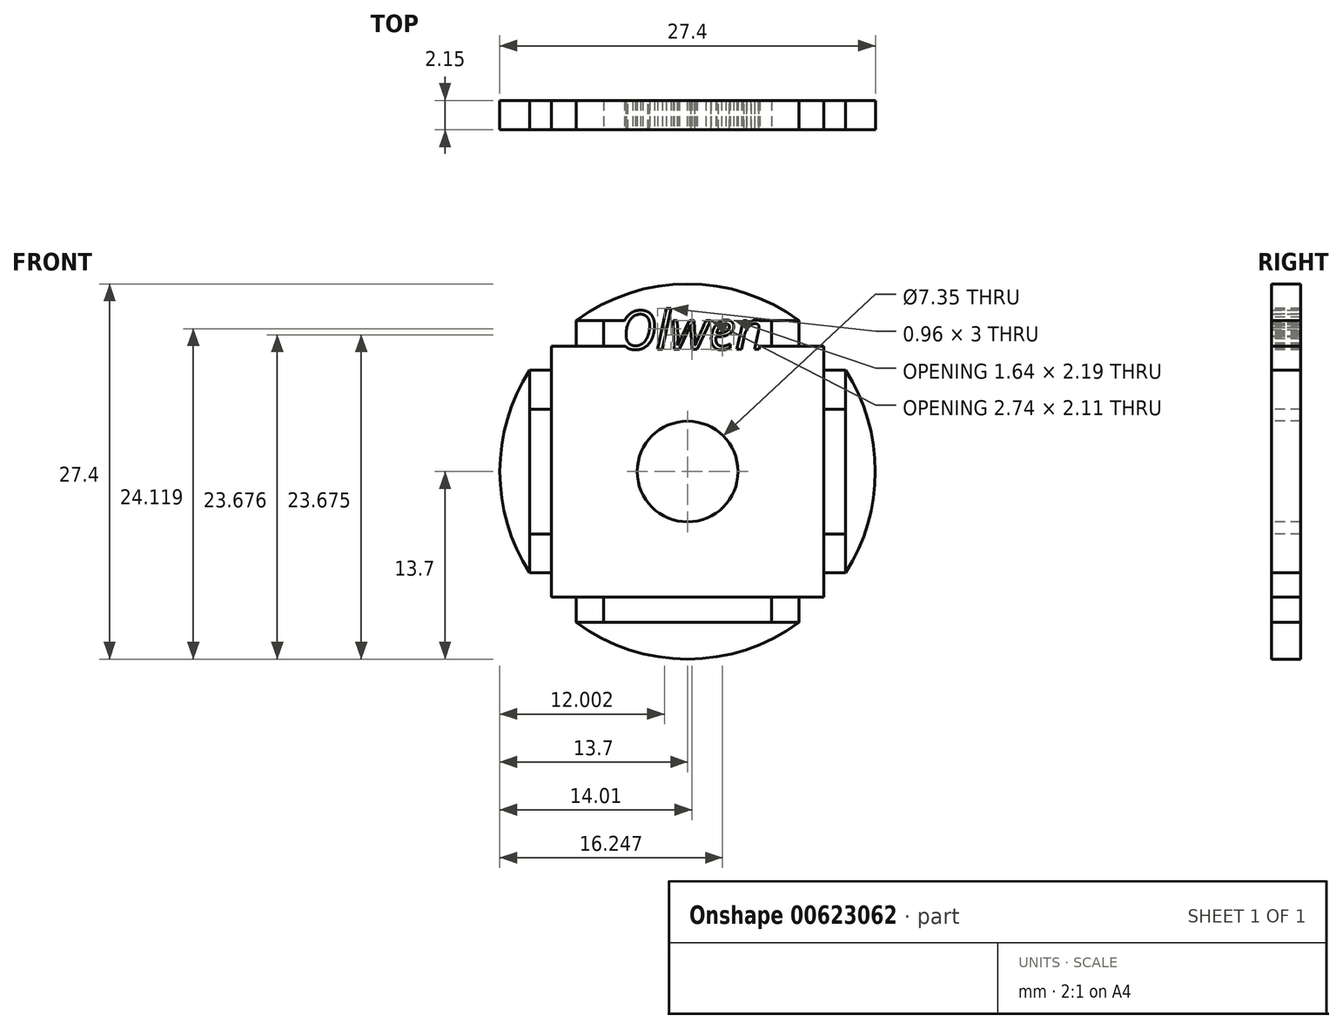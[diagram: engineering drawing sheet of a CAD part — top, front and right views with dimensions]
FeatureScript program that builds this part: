
annotation { "Feature Type Name" : "Feature", "Feature Type Description" : "" }
export const myFeature = defineFeature(function(context is Context, id is Id, definition is map)
    precondition{}
    {
        {
            var Q0;
            Q0=qCreatedBy(makeId("Front.planeOp"),FACE);
            var sketch = newSketch(context, id + "F0", { "sketchPlane" : qUnion([Q0])});
            skCircle(sketch, "E0", {"center": v(0, 0) * mm, "radius": 13.7 * mm});
            skSolve(sketch);
        }
        {
            var Q0;
            Q0=makeQuery(id+"F0.imprint","IMPRINT",FACE,{"disambiguationData":[TD([[makeQuery(id+"F0.imprint","IMPRINT",EDGE,{"derivedFrom":sQuery(id+"F0.wireOp",EDGE,"E0")}),1.0]])]});
            extrude(context, id + "F1", {"entities" : qUnion([Q0]), "depth" : 2.15 * mm, "offsetDistance" : 25 * mm});
        }
        {
            var Q0;
            Q0=makeQuery(id+"F1.opExtrude","CAP_FACE",FACE,{"disambiguationData":[OSD([sQuery(id+"F0.wireOp",EDGE,"E0")])],"isStart":false});
            var sketch = newSketch(context, id + "F2", { "sketchPlane" : qUnion([Q0])});
            skText(sketch, "E1", { "text": "Olwen", "fontName": "OpenSans-Italic.ttf"});
            const initialGuessF2  = {"E1": [-0.00513, 0.00892, 1, 0, 0.00284]};
            skSetInitialGuess(sketch, initialGuessF2);
            skSolve(sketch);
        }
        {
            var Q0;
            Q0 = qSketchRegion(id + "F2", true);
            extrude(context, id + "F3", {"entities" : qUnion([Q0]), "operationType" : NewBodyOperationType.REMOVE, "endBound" : BoundingType.UP_TO_NEXT, "oppositeDirection" : true, "depth" : 25 * mm, "offsetDistance" : 25 * mm});
        }
        {
            var Q0;
            {var subQ0=sQuery(id+"F0.wireOp",EDGE,"E0");Q0=makeQuery(id+"F3.boolean.opBoolean","SPLIT",FACE,{"disambiguationData":[TD([makeQuery(id+"F1.opExtrude","SWEPT_FACE",FACE,{"disambiguationData":[OSD([subQ0])]})])],"derivedFrom":makeQuery(id+"F1.opExtrude","CAP_FACE",FACE,{"disambiguationData":[OSD([subQ0])],"isStart":false})});}
            var sketch = newSketch(context, id + "F4", { "sketchPlane" : qUnion([Q0])});
            skCircle(sketch, "E2", {"center": v(0, 0) * mm, "radius": 3.68 * mm});
            skLineSegment(sketch, "E3.bottom", {"start": v(-6.75, 4.44) * mm, "end": v(6.75, 4.44) * mm});
            skLineSegment(sketch, "E3.top", {"start": v(-6.75, -4.44) * mm, "end": v(6.75, -4.44) * mm});
            skLineSegment(sketch, "E3.left", {"start": v(-6.75, 4.44) * mm, "end": v(-6.75, -4.44) * mm});
            skLineSegment(sketch, "E3.right", {"start": v(6.75, 4.44) * mm, "end": v(6.75, -4.44) * mm});
            skLineSegment(sketch, "E4.bottom", {"start": v(-1, 2.86) * mm, "end": v(1, 2.86) * mm});
            skLineSegment(sketch, "E4.top", {"start": v(-1, -2.86) * mm, "end": v(1, -2.86) * mm});
            skLineSegment(sketch, "E4.left", {"start": v(-1, 2.86) * mm, "end": v(-1, -2.86) * mm});
            skLineSegment(sketch, "E4.right", {"start": v(1, 2.86) * mm, "end": v(1, -2.86) * mm});
            skLineSegment(sketch, "E5.bottom", {"start": v(-8.86, 6.74) * mm, "end": v(8.86, 6.74) * mm});
            skLineSegment(sketch, "E5.top", {"start": v(-8.86, -6.74) * mm, "end": v(8.86, -6.74) * mm});
            skLineSegment(sketch, "E5.left", {"start": v(-8.86, 6.74) * mm, "end": v(-8.86, -6.74) * mm});
            skLineSegment(sketch, "E5.right", {"start": v(8.86, 6.74) * mm, "end": v(8.86, -6.74) * mm});
            skSolve(sketch);
        }
        {
            var Q0;
            Q0=makeQuery(id+"F4.imprint","IMPRINT",FACE,{"disambiguationData":[TD([[makeQuery(id+"F4.imprint","IMPRINT",EDGE,{"derivedFrom":sQuery(id+"F4.wireOp",EDGE,"E2")}),1.0]])]});
            var Q1;
            Q1=makeQuery(id+"F4.imprint","IMPRINT",FACE,{"disambiguationData":[TD([[makeQuery(id+"F4.imprint","IMPRINT",EDGE,{"derivedFrom":sQuery(id+"F4.wireOp",EDGE,"E4.bottom")}),-1.0]])]});
            extrude(context, id + "F5", {"entities" : qUnion([Q0, Q1]), "operationType" : NewBodyOperationType.REMOVE, "endBound" : BoundingType.UP_TO_NEXT, "oppositeDirection" : true, "depth" : 25 * mm, "offsetDistance" : 25 * mm});
        }
        {
            var Q0;
            {var subQ0=sQuery(id+"F0.wireOp",EDGE,"E0");Q0=makeQuery(id+"F3.boolean.opBoolean","SPLIT",FACE,{"disambiguationData":[TD([makeQuery(id+"F1.opExtrude","SWEPT_FACE",FACE,{"disambiguationData":[OSD([subQ0])]})])],"derivedFrom":makeQuery(id+"F1.opExtrude","CAP_FACE",FACE,{"disambiguationData":[OSD([subQ0])],"isStart":false})});}
            var sketch = newSketch(context, id + "F6", { "sketchPlane" : qUnion([Q0])});
            skLineSegment(sketch, "E6.bottom", {"start": v(-5.33, 4.8) * mm, "end": v(5.33, 4.8) * mm});
            skLineSegment(sketch, "E6.top", {"start": v(-5.33, -4.8) * mm, "end": v(5.33, -4.8) * mm});
            skLineSegment(sketch, "E6.left", {"start": v(-5.33, 4.8) * mm, "end": v(-5.33, -4.8) * mm});
            skLineSegment(sketch, "E6.right", {"start": v(5.33, 4.8) * mm, "end": v(5.33, -4.8) * mm});
            skPoint(sketch, "E6.middle", {"position": v(0, 0) * mm});
            skSolve(sketch);
        }
        {
            var Q0;
            {var subQ0=sQuery(id+"F0.wireOp",EDGE,"E0");Q0=makeQuery(id+"F3.boolean.opBoolean","SPLIT",FACE,{"disambiguationData":[TD([makeQuery(id+"F1.opExtrude","SWEPT_FACE",FACE,{"disambiguationData":[OSD([subQ0])]})])],"derivedFrom":makeQuery(id+"F1.opExtrude","CAP_FACE",FACE,{"disambiguationData":[OSD([subQ0])],"isStart":false})});}
            var sketch = newSketch(context, id + "F7", { "sketchPlane" : qUnion([Q0])});
            skLineSegment(sketch, "E7.0", {"start": v(-11.53, 11.03) * mm, "end": v(-11.53, -11.03) * mm});
            skLineSegment(sketch, "E7.1", {"start": v(11.53, 11.03) * mm, "end": v(-11.53, 11.03) * mm});
            skLineSegment(sketch, "E7.2", {"start": v(11.53, -11.03) * mm, "end": v(11.53, 11.03) * mm});
            skLineSegment(sketch, "E7.3", {"start": v(-11.53, -11.03) * mm, "end": v(11.53, -11.03) * mm});
            skSolve(sketch);
        }
        {
            var Q0;
            {var subQ3=makeQuery(id+"F3.boolean.opBoolean","COPY",EDGE,{"derivedFrom":makeQuery(id+"F3.opExtrude","CAP_EDGE",EDGE,{"disambiguationData":[OSD([sQuery(id+"F2.wireOp",EDGE,"E1.sketch_text.stroke-0")])],"isStart":true})});Q0=makeQuery(id+"F7.imprint","IMPRINT",FACE,{"disambiguationData":[TD([[makeQuery(id+"F7.imprint","IMPRINT",EDGE,{"derivedFrom":subQ3}),1.0]])]});}
            var sketch = newSketch(context, id + "F8", { "sketchPlane" : qUnion([Q0])});
            skLineSegment(sketch, "E8.bottom", {"start": v(-9.94, 9.16) * mm, "end": v(9.94, 9.16) * mm});
            skLineSegment(sketch, "E8.top", {"start": v(-9.94, -9.16) * mm, "end": v(9.94, -9.16) * mm});
            skLineSegment(sketch, "E8.left", {"start": v(-9.94, 9.16) * mm, "end": v(-9.94, -9.16) * mm});
            skLineSegment(sketch, "E8.right", {"start": v(9.94, 9.16) * mm, "end": v(9.94, -9.16) * mm});
            skPoint(sketch, "E8.middle", {"position": v(0, 0) * mm});
            skSolve(sketch);
        }
        {
            var Q0;
            Q0=makeQuery(id+"F8.imprint","IMPRINT",FACE,{"disambiguationData":[TD([[makeQuery(id+"F8.imprint","IMPRINT",EDGE,{"derivedFrom":sQuery(id+"F8.wireOp",EDGE,"E8.top")}),-1.0]])]});
            extrude(context, id + "F9", {"entities" : qUnion([Q0]), "operationType" : NewBodyOperationType.REMOVE, "endBound" : BoundingType.UP_TO_NEXT, "oppositeDirection" : true, "depth" : 25 * mm, "offsetDistance" : 25 * mm});
        }
        {
            var Q0;
            Q0=makeQuery(id+"F6.imprint","IMPRINT",FACE,{"disambiguationData":[TD([[makeQuery(id+"F6.imprint","IMPRINT",EDGE,{"derivedFrom":sQuery(id+"F6.wireOp",EDGE,"E6.bottom")}),1.0]])]});
            var sketch = newSketch(context, id + "F10", { "sketchPlane" : qUnion([Q0])});
            skLineSegment(sketch, "E9.bottom", {"start": v(-11.53, 7.4) * mm, "end": v(-9.94, 7.4) * mm});
            skLineSegment(sketch, "E9.top", {"start": v(-11.53, 4.56) * mm, "end": v(-9.94, 4.56) * mm});
            skLineSegment(sketch, "E9.left", {"start": v(-11.53, 7.4) * mm, "end": v(-11.53, 4.56) * mm});
            skLineSegment(sketch, "E9.right", {"start": v(-9.94, 7.4) * mm, "end": v(-9.94, 4.56) * mm});
            skLineSegment(sketch, "E10.MirrorCS", {"start": v(-11.53, -4.56) * mm, "end": v(-9.94, -4.56) * mm});
            skLineSegment(sketch, "E11.MirrorCS", {"start": v(-11.53, -7.4) * mm, "end": v(-9.94, -7.4) * mm});
            skLineSegment(sketch, "E12.MirrorCS", {"start": v(-9.94, -7.4) * mm, "end": v(-9.94, -4.56) * mm});
            skLineSegment(sketch, "E13.MirrorCS", {"start": v(-11.53, -7.4) * mm, "end": v(-11.53, -4.56) * mm});
            skLineSegment(sketch, "E14.MirrorCS", {"start": v(11.53, 7.4) * mm, "end": v(9.94, 7.4) * mm});
            skLineSegment(sketch, "E15.MirrorCS", {"start": v(11.53, -7.4) * mm, "end": v(11.53, -4.56) * mm});
            skLineSegment(sketch, "E16.MirrorCS", {"start": v(11.53, 4.56) * mm, "end": v(9.94, 4.56) * mm});
            skLineSegment(sketch, "E17.MirrorCS", {"start": v(9.94, 7.4) * mm, "end": v(9.94, 4.56) * mm});
            skLineSegment(sketch, "E18.MirrorCS", {"start": v(11.53, -4.56) * mm, "end": v(9.94, -4.56) * mm});
            skLineSegment(sketch, "E19.MirrorCS", {"start": v(11.53, -7.4) * mm, "end": v(9.94, -7.4) * mm});
            skLineSegment(sketch, "E20.MirrorCS", {"start": v(9.94, -7.4) * mm, "end": v(9.94, -4.56) * mm});
            skLineSegment(sketch, "E21.MirrorCS", {"start": v(11.53, 7.4) * mm, "end": v(11.53, 4.56) * mm});
            skSolve(sketch);
        }
        {
            var Q0;
            Q0=makeQuery(id+"F6.imprint","IMPRINT",FACE,{"disambiguationData":[TD([[makeQuery(id+"F6.imprint","IMPRINT",EDGE,{"derivedFrom":sQuery(id+"F6.wireOp",EDGE,"E6.bottom")}),1.0]])]});
            var sketch = newSketch(context, id + "F11", { "sketchPlane" : qUnion([Q0])});
            skLineSegment(sketch, "E22", {"start": v(-8.13, -9.16) * mm, "end": v(-6.13, -9.16) * mm});
            skLineSegment(sketch, "E23", {"start": v(-8.13, -9.16) * mm, "end": v(-8.13, -11.03) * mm});
            skLineSegment(sketch, "E24", {"start": v(-8.13, -11.03) * mm, "end": v(-6.13, -11.03) * mm});
            skLineSegment(sketch, "E25", {"start": v(-6.13, -11.03) * mm, "end": v(-6.13, -9.16) * mm});
            skLineSegment(sketch, "E26.MirrorCS", {"start": v(6.13, -11.03) * mm, "end": v(6.13, -9.16) * mm});
            skLineSegment(sketch, "E27.MirrorCS", {"start": v(8.13, -9.16) * mm, "end": v(6.13, -9.16) * mm});
            skLineSegment(sketch, "E28.MirrorCS", {"start": v(8.13, -11.03) * mm, "end": v(6.13, -11.03) * mm});
            skLineSegment(sketch, "E29.MirrorCS", {"start": v(8.13, -9.16) * mm, "end": v(8.13, -11.03) * mm});
            skLineSegment(sketch, "E30.MirrorCS", {"start": v(8.13, 9.16) * mm, "end": v(6.13, 9.16) * mm});
            skLineSegment(sketch, "E31.MirrorCS", {"start": v(6.13, 11.03) * mm, "end": v(6.13, 9.16) * mm});
            skLineSegment(sketch, "E32.MirrorCS", {"start": v(-6.13, 11.03) * mm, "end": v(-6.13, 9.16) * mm});
            skLineSegment(sketch, "E33.MirrorCS", {"start": v(-8.13, 9.16) * mm, "end": v(-6.13, 9.16) * mm});
            skLineSegment(sketch, "E34.MirrorCS", {"start": v(8.13, 9.16) * mm, "end": v(8.13, 11.03) * mm});
            skLineSegment(sketch, "E35.MirrorCS", {"start": v(-8.13, 11.03) * mm, "end": v(-6.13, 11.03) * mm});
            skLineSegment(sketch, "E36.MirrorCS", {"start": v(8.13, 11.03) * mm, "end": v(6.13, 11.03) * mm});
            skLineSegment(sketch, "E37.MirrorCS", {"start": v(-8.13, 9.16) * mm, "end": v(-8.13, 11.03) * mm});
            skSolve(sketch);
        }
        {
            var Q0;
            Q0 = qSketchRegion(id + "F10", true);
            extrude(context, id + "F12", {"entities" : qUnion([Q0]), "oppositeDirection" : true, "depth" : 2.15 * mm, "offsetDistance" : 25 * mm});
        }
        {
            var Q0;
            Q0 = qSketchRegion(id + "F11", true);
            extrude(context, id + "F13", {"entities" : qUnion([Q0]), "oppositeDirection" : true, "depth" : 2.15 * mm, "offsetDistance" : 25 * mm});
        }
    });
